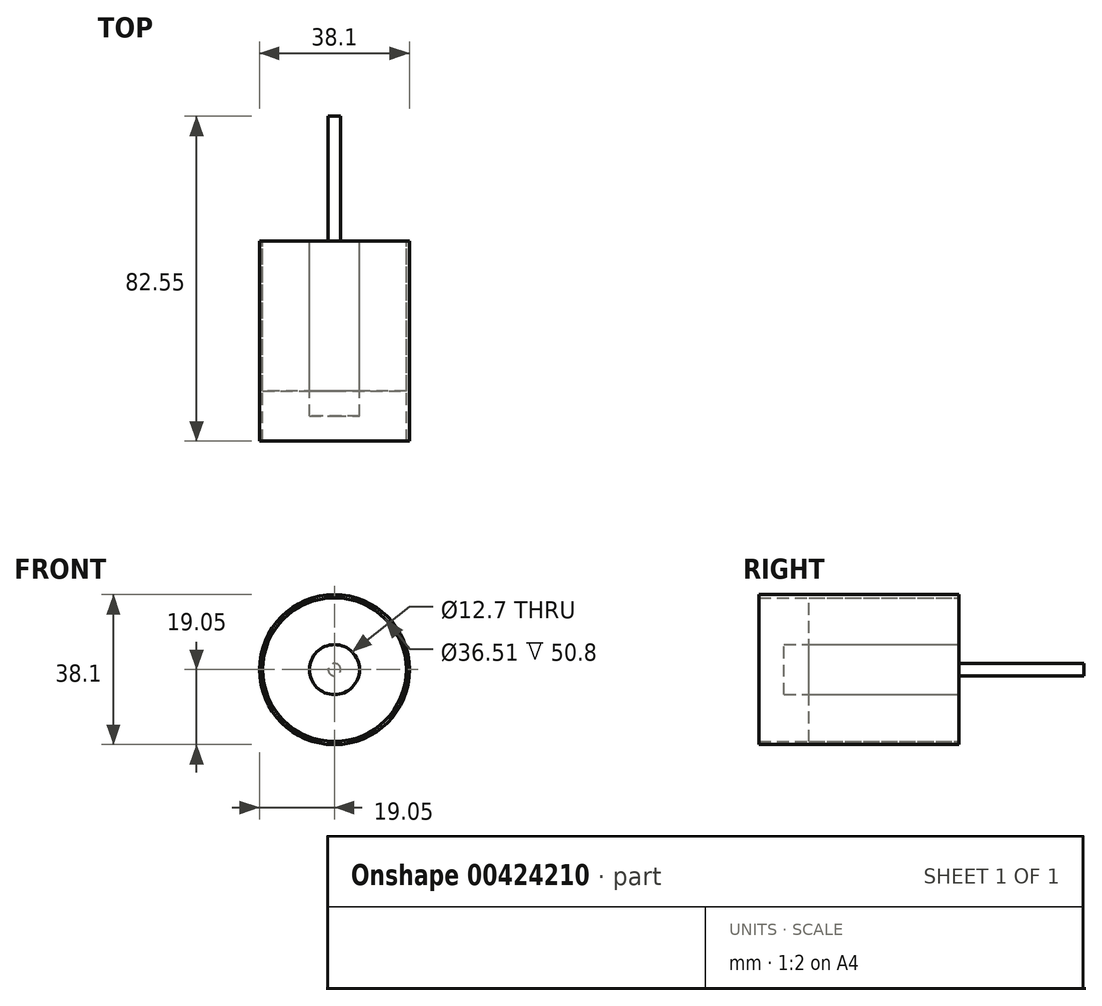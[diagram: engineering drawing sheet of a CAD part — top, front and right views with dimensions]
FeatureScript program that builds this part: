
annotation { "Feature Type Name" : "Feature", "Feature Type Description" : "" }
export const myFeature = defineFeature(function(context is Context, id is Id, definition is map)
    precondition{}
    {
        {
            var Q0;
            Q0=qCreatedBy(makeId("Front.planeOp"),FACE);
            var sketch = newSketch(context, id + "F0", { "sketchPlane" : qUnion([Q0])});
            skCircle(sketch, "E0", {"center": v(0, 0) * mm, "radius": 19.05 * mm});
            skCircle(sketch, "E1", {"center": v(0, 0) * mm, "radius": 6.35 * mm});
            skCircle(sketch, "E2", {"center": v(0, 0) * mm, "radius": 18.26 * mm});
            skSolve(sketch);
        }
        {
            var Q0;
            Q0 = qSketchRegion(id + "F0", true);
            extrude(context, id + "F1", {"entities" : qUnion([Q0]), "depth" : 50.8 * mm});
        }
        {
            var Q0;
            Q0=qCreatedBy(makeId("Front.planeOp"),FACE);
            var sketch = newSketch(context, id + "F2", { "sketchPlane" : qUnion([Q0])});
            skCircle(sketch, "E3", {"center": v(0, 0) * mm, "radius": 6.35 * mm});
            skSolve(sketch);
        }
        {
            var Q0;
            Q0 = qSketchRegion(id + "F2", true);
            extrude(context, id + "F3", {"entities" : qUnion([Q0]), "operationType" : NewBodyOperationType.ADD, "depth" : 44.45 * mm});
        }
        {
            var Q0;
            Q0=makeQuery(id+"F0.imprint","IMPRINT",FACE,{"disambiguationData":[TD([[makeQuery(id+"F0.imprint","IMPRINT",EDGE,{"derivedFrom":sQuery(id+"F0.wireOp",EDGE,"E1")}),-1.0]])]});
            extrude(context, id + "F4", {"entities" : qUnion([Q0]), "depth" : 38.1 * mm});
        }
        {
            var Q0;
            Q0=qCreatedBy(makeId("Front.planeOp"),FACE);
            var sketch = newSketch(context, id + "F5", { "sketchPlane" : qUnion([Q0])});
            skCircle(sketch, "E4", {"center": v(0, 0) * mm, "radius": 1.59 * mm});
            skSolve(sketch);
        }
        {
            var Q0;
            Q0 = qSketchRegion(id + "F5", true);
            extrude(context, id + "F6", {"entities" : qUnion([Q0]), "operationType" : NewBodyOperationType.ADD, "oppositeDirection" : true, "depth" : 31.75 * mm});
        }
    });
